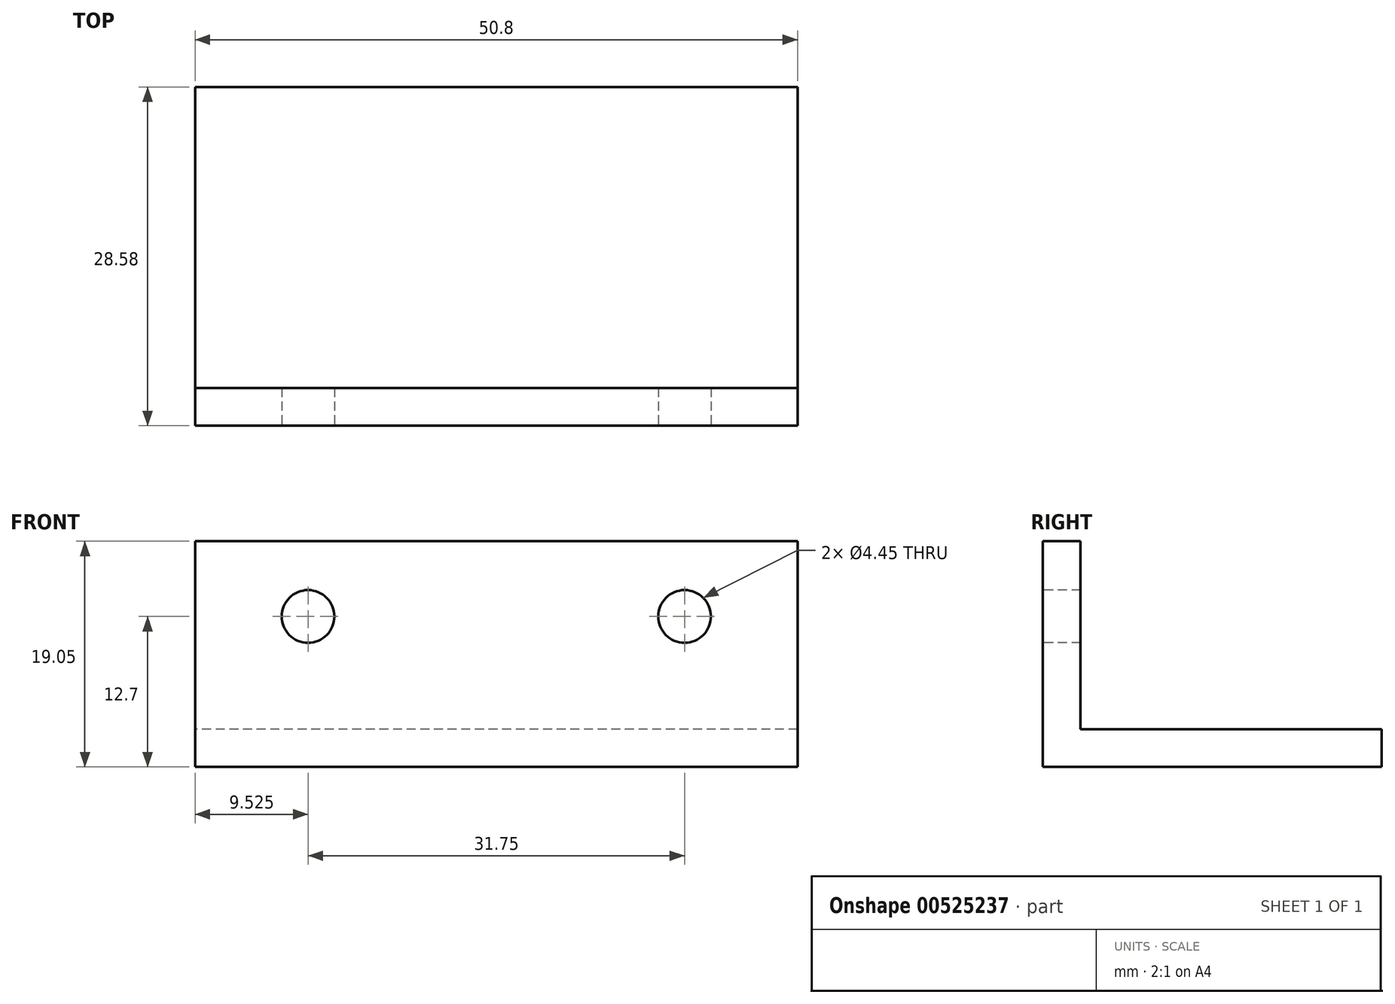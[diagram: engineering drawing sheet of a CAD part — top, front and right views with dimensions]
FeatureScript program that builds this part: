
annotation { "Feature Type Name" : "Feature", "Feature Type Description" : "" }
export const myFeature = defineFeature(function(context is Context, id is Id, definition is map)
    precondition{}
    {
        {
            var Q0;
            Q0=qCreatedBy(makeId("Top.planeOp"),FACE);
            var sketch = newSketch(context, id + "F0", { "sketchPlane" : qUnion([Q0])});
            skLineSegment(sketch, "E0.bottom", {"start": v(25.4, 12.7) * mm, "end": v(-25.4, 12.7) * mm});
            skLineSegment(sketch, "E0.top", {"start": v(25.4, -12.7) * mm, "end": v(-25.4, -12.7) * mm});
            skLineSegment(sketch, "E0.left", {"start": v(25.4, 12.7) * mm, "end": v(25.4, -12.7) * mm});
            skLineSegment(sketch, "E0.right", {"start": v(-25.4, 12.7) * mm, "end": v(-25.4, -12.7) * mm});
            skPoint(sketch, "E0.middle", {"position": v(0, 0) * mm});
            skSolve(sketch);
        }
        {
            var Q0;
            Q0 = qSketchRegion(id + "F0", true);
            extrude(context, id + "F1", {"entities" : qUnion([Q0]), "depth" : 3.17 * mm, "offsetDistance" : 25.4 * mm});
        }
        {
            var Q0;
            Q0=makeQuery(id+"F1.opExtrude","SWEPT_FACE",FACE,{"disambiguationData":[OSD([sQuery(id+"F0.wireOp",EDGE,"E0.top")])]});
            var sketch = newSketch(context, id + "F2", { "sketchPlane" : qUnion([Q0])});
            skLineSegment(sketch, "E1.bottom", {"start": v(-25.4, 0) * mm, "end": v(25.4, 0) * mm});
            skLineSegment(sketch, "E1.top", {"start": v(-25.4, 19.05) * mm, "end": v(25.4, 19.05) * mm});
            skLineSegment(sketch, "E1.left", {"start": v(-25.4, 0) * mm, "end": v(-25.4, 19.05) * mm});
            skLineSegment(sketch, "E1.right", {"start": v(25.4, 0) * mm, "end": v(25.4, 19.05) * mm});
            skSolve(sketch);
        }
        {
            var Q0;
            Q0 = qSketchRegion(id + "F2", true);
            extrude(context, id + "F3", {"entities" : qUnion([Q0]), "operationType" : NewBodyOperationType.ADD, "depth" : 3.17 * mm, "offsetDistance" : 25.4 * mm});
        }
        {
            var Q0;
            Q0=makeQuery(id+"F3.opExtrude","CAP_FACE",FACE,{"disambiguationData":[OSD([sQuery(id+"F2.wireOp",EDGE,"E1.bottom"),sQuery(id+"F2.wireOp",EDGE,"E1.top"),sQuery(id+"F2.wireOp",EDGE,"E1.left"),sQuery(id+"F2.wireOp",EDGE,"E1.right")])],"isStart":false});
            var sketch = newSketch(context, id + "F4", { "sketchPlane" : qUnion([Q0])});
            skSolve(sketch);
        }
        {
            var Q0;
            Q0=makeQuery(id+"F4.imprint","IMPRINT",FACE,{"disambiguationData":[TD([[makeQuery(id+"F4.imprint","IMPRINT",EDGE,{"derivedFrom":makeQuery(id+"F3.opExtrude","CAP_EDGE",EDGE,{"disambiguationData":[OSD([sQuery(id+"F2.wireOp",EDGE,"E1.bottom")])],"isStart":false})}),-1.0]])]});
            var sketch = newSketch(context, id + "F5", { "sketchPlane" : qUnion([Q0])});
            skCircle(sketch, "E2", {"center": v(15.88, 12.7) * mm, "radius": 2.22 * mm});
            skCircle(sketch, "E3.MirrorC", {"center": v(-15.88, 12.7) * mm, "radius": 2.22 * mm});
            skSolve(sketch);
        }
        {
            var Q0;
            Q0=sQuery(id+"F5.wireOp",VERTEX,"E2.center");
            var Q1;
            Q1=makeQuery(id+"F1.opExtrude","SWEPT_BODY",BODY,{"disambiguationData":[OSD([sQuery(id+"F0.wireOp",EDGE,"E0.bottom"),sQuery(id+"F0.wireOp",EDGE,"E0.top"),sQuery(id+"F0.wireOp",EDGE,"E0.left"),sQuery(id+"F0.wireOp",EDGE,"E0.right")])]});
            hole(context, id + "F6", {"style" : HoleStyle.SIMPLE, "endStyle" : HoleEndStyle.THROUGH, "holeDiameter" : 4.44 * mm, "isTappedThrough" : true, "tappedDepth" : 12.7 * mm, "tapClearance" : 3, "locations" : qUnion([Q0]), "scope" : qUnion([Q1])});
        }
        {
            var Q0;
            Q0=makeQuery(id+"F4.imprint","IMPRINT",FACE,{"disambiguationData":[TD([[makeQuery(id+"F4.imprint","IMPRINT",EDGE,{"derivedFrom":makeQuery(id+"F3.opExtrude","CAP_EDGE",EDGE,{"disambiguationData":[OSD([sQuery(id+"F2.wireOp",EDGE,"E1.bottom")])],"isStart":false})}),-1.0]])]});
            var sketch = newSketch(context, id + "F7", { "sketchPlane" : qUnion([Q0])});
            skPoint(sketch, "E4", {"position": v(-15.88, 12.7) * mm});
            skSolve(sketch);
        }
        {
            var Q0;
            Q0=sQuery(id+"F7.wireOp",VERTEX,"E4");
            var Q1;
            Q1=makeQuery(id+"F1.opExtrude","SWEPT_BODY",BODY,{"disambiguationData":[OSD([sQuery(id+"F0.wireOp",EDGE,"E0.bottom"),sQuery(id+"F0.wireOp",EDGE,"E0.top"),sQuery(id+"F0.wireOp",EDGE,"E0.left"),sQuery(id+"F0.wireOp",EDGE,"E0.right")])]});
            hole(context, id + "F8", {"style" : HoleStyle.SIMPLE, "endStyle" : HoleEndStyle.THROUGH, "holeDiameter" : 4.44 * mm, "isTappedThrough" : true, "tappedDepth" : 12.7 * mm, "tapClearance" : 3, "locations" : qUnion([Q0]), "scope" : qUnion([Q1])});
        }
    });
